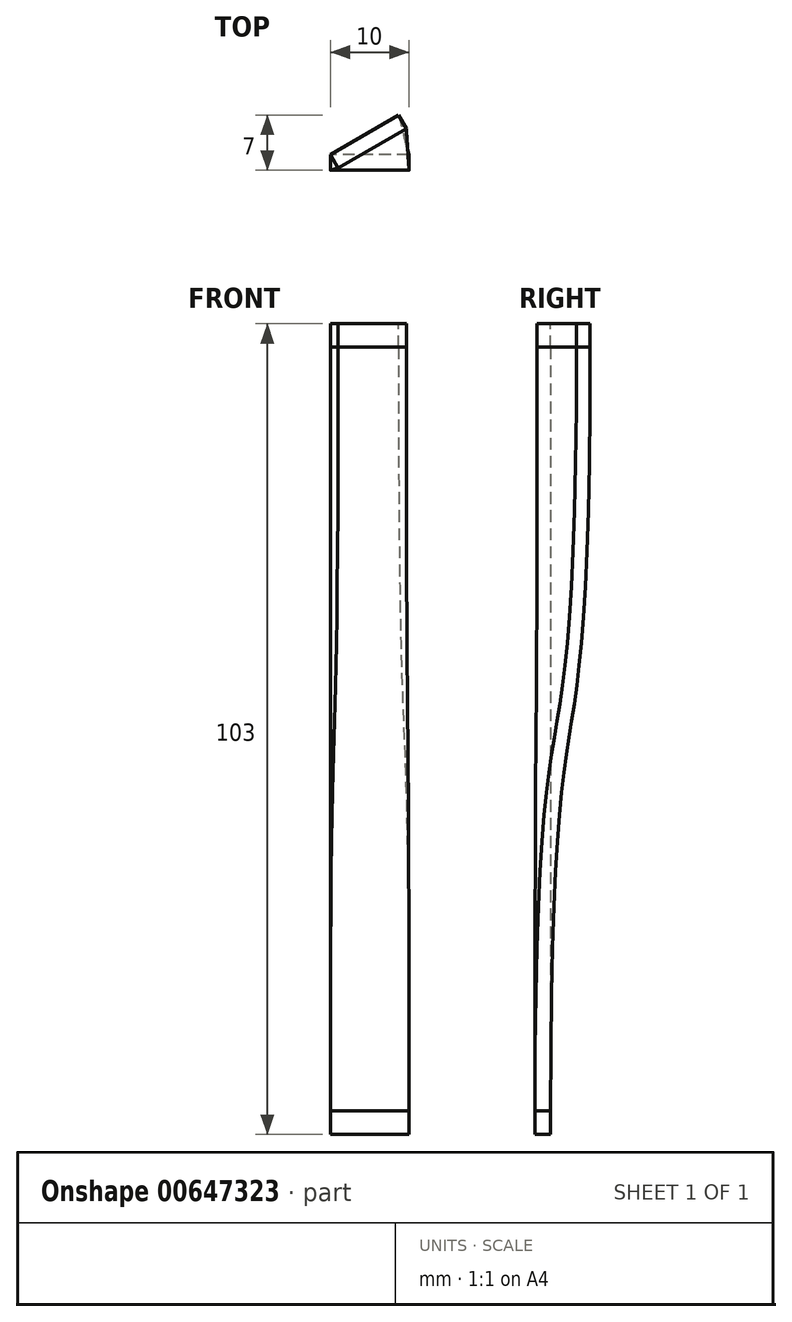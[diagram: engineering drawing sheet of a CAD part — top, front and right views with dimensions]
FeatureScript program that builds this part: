
annotation { "Feature Type Name" : "Feature", "Feature Type Description" : "" }
export const myFeature = defineFeature(function(context is Context, id is Id, definition is map)
    precondition{}
    {
        {
            var Q0;
            Q0=qCreatedBy(makeId("Top.planeOp"),FACE);
            var sketch = newSketch(context, id + "F0", { "sketchPlane" : qUnion([Q0])});
            skLineSegment(sketch, "E0", {"start": v(0, 0) * mm, "end": v(5, 0) * mm, "construction": true});
            skLineSegment(sketch, "E1", {"start": v(5, 0) * mm, "end": v(5, 1) * mm, "construction": true});
            skLineSegment(sketch, "E2", {"start": v(-5, 0) * mm, "end": v(-5, -1) * mm, "construction": true});
            skLineSegment(sketch, "E3.bottom", {"start": v(5, 1) * mm, "end": v(-5, 1) * mm});
            skLineSegment(sketch, "E3.top", {"start": v(5, -1) * mm, "end": v(-5, -1) * mm});
            skLineSegment(sketch, "E3.left", {"start": v(5, 1) * mm, "end": v(5, -1) * mm});
            skLineSegment(sketch, "E3.right", {"start": v(-5, 1) * mm, "end": v(-5, -1) * mm});
            skLineSegment(sketch, "E4.MirrorCS", {"start": v(0, 0) * mm, "end": v(-5, 0) * mm, "construction": true});
            skSolve(sketch);
        }
        {
            var Q0;
            Q0=makeQuery(id+"F0.imprint","IMPRINT",FACE,{"disambiguationData":[TD([[makeQuery(id+"F0.imprint","IMPRINT",EDGE,{"derivedFrom":sQuery(id+"F0.wireOp",EDGE,"E3.bottom")}),1.0]])]});
            extrude(context, id + "F1", {"entities" : qUnion([Q0]), "depth" : 3 * mm, "offsetDistance" : 25 * mm});
        }
        {
            var Q0;
            Q0=makeQuery(id+"F1.opExtrude","CAP_FACE",FACE,{"disambiguationData":[OSD([sQuery(id+"F0.wireOp",EDGE,"E3.bottom"),sQuery(id+"F0.wireOp",EDGE,"E3.top"),sQuery(id+"F0.wireOp",EDGE,"E3.left"),sQuery(id+"F0.wireOp",EDGE,"E3.right")])],"isStart":false});
            var sketch = newSketch(context, id + "F2", { "sketchPlane" : qUnion([Q0])});
            skLineSegment(sketch, "E5", {"start": v(-5, 0) * mm, "end": v(5, 0) * mm, "construction": true});
            skLineSegment(sketch, "E6", {"start": v(0, 1) * mm, "end": v(0, -1) * mm, "construction": true});
            skSolve(sketch);
        }
        {
            var Q0;
            Q0=makeQuery(id+"F2.imprint","IMPRINT",FACE,{"disambiguationData":[TD([[makeQuery(id+"F2.imprint","IMPRINT",EDGE,{"derivedFrom":makeQuery(id+"F1.opExtrude","CAP_EDGE",EDGE,{"disambiguationData":[OSD([sQuery(id+"F0.wireOp",EDGE,"E3.bottom")])],"isStart":false})}),1.0]])]});
            cPlane(context, id + "F3", {"entities" : qUnion([Q0]), "cplaneType" : CPlaneType.OFFSET, "offset" : 100 * mm, "width" : 150 * mm, "height" : 150 * mm});
        }
        {
            var Q0;
            Q0=qCreatedBy(id+"F3.planeOp",FACE);
            var sketch = newSketch(context, id + "F4", { "sketchPlane" : qUnion([Q0])});
            skLineSegment(sketch, "E7", {"start": v(0, 0) * mm, "end": v(0, 1) * mm, "construction": true});
            skLineSegment(sketch, "E8.MirrorCS", {"start": v(0, 0) * mm, "end": v(0, -1) * mm, "construction": true});
            skLineSegment(sketch, "E9", {"start": v(0, 1) * mm, "end": v(5, 1) * mm, "construction": true});
            skLineSegment(sketch, "E10", {"start": v(0, -1) * mm, "end": v(-5, -1) * mm, "construction": true});
            skLineSegment(sketch, "E11.bottom", {"start": v(5, 1) * mm, "end": v(-5, 1) * mm});
            skLineSegment(sketch, "E11.top", {"start": v(5, -1) * mm, "end": v(-5, -1) * mm});
            skLineSegment(sketch, "E11.left", {"start": v(5, 1) * mm, "end": v(5, -1) * mm});
            skLineSegment(sketch, "E11.right", {"start": v(-5, 1) * mm, "end": v(-5, -1) * mm});
            skSolve(sketch);
        }
        {
            var Q0;
            Q0=makeQuery(id+"F4.imprint","IMPRINT",FACE,{"disambiguationData":[TD([[makeQuery(id+"F4.imprint","IMPRINT",EDGE,{"derivedFrom":sQuery(id+"F4.wireOp",EDGE,"E11.bottom")}),1.0]])]});
            extrude(context, id + "F5", {"entities" : qUnion([Q0]), "oppositeDirection" : true, "depth" : 3 * mm, "offsetDistance" : 25 * mm});
        }
        {
            var Q0;
            Q0=makeQuery(id+"F5.opExtrude","SWEPT_BODY",BODY,{"disambiguationData":[OSD([sQuery(id+"F4.wireOp",EDGE,"E11.bottom"),sQuery(id+"F4.wireOp",EDGE,"E11.top"),sQuery(id+"F4.wireOp",EDGE,"E11.left"),sQuery(id+"F4.wireOp",EDGE,"E11.right")])]});
            var Q1;
            Q1=makeQuery(id+"F5.opExtrude","SWEPT_EDGE",EDGE,{"disambiguationData":[OSD([sQuery(id+"F4.wireOp",EDGE,"E11.bottom"),sQuery(id+"F4.wireOp",EDGE,"E11.right")])]});
            transform(context, id + "F6", {"entities" : qUnion([Q0]), "transformType" : TransformType.ROTATION, "transformAxis" : qUnion([Q1]), "angle" : 30 * degree, "makeCopy" : false});
        }
        {
            var Q0;
            Q0=makeQuery(id+"F5.opExtrude","CAP_FACE",FACE,{"disambiguationData":[OSD([sQuery(id+"F4.wireOp",EDGE,"E11.bottom"),sQuery(id+"F4.wireOp",EDGE,"E11.top"),sQuery(id+"F4.wireOp",EDGE,"E11.left"),sQuery(id+"F4.wireOp",EDGE,"E11.right")])],"isStart":false});
            var Q1;
            Q1=makeQuery(id+"F2.imprint","IMPRINT",FACE,{"disambiguationData":[TD([[makeQuery(id+"F2.imprint","IMPRINT",EDGE,{"derivedFrom":makeQuery(id+"F1.opExtrude","CAP_EDGE",EDGE,{"disambiguationData":[OSD([sQuery(id+"F0.wireOp",EDGE,"E3.bottom")])],"isStart":false})}),1.0]])]});
            loft(context, id + "F7", {"startCondition" : LoftEndDerivativeType.NORMAL_TO_PROFILE, "startMagnitude" : 2, "endCondition" : LoftEndDerivativeType.NORMAL_TO_PROFILE, "endMagnitude" : 2, "sheetProfilesArray" : [{ "sheetProfileEntities" : qUnion([Q0]) }, { "sheetProfileEntities" : qUnion([Q1]) }]});
        }
    });
